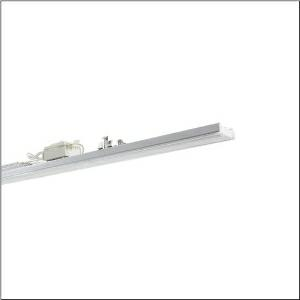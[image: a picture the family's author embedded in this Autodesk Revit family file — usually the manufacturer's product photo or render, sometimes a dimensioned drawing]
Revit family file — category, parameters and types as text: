
# Revit family: licross_r__21_recessed_ho_52te1edn4e5s_6cbf
name_source: partatom
category: Lighting Fixtures
units: mm (PartAtom-declared; Revit-internal decimal feet)

## family parameters
Cut with Voids When Loaded = No
Host = Face
Light Source = No
Part Type = Normal
Room Calculation Point = No
Round Connector Dimension = Use Diameter
Shared = No

## types (1)
- --- (1 x LED, 14620 lm, 84.6 W, 4000K)
    Apparent Load = 85 VA
    CIE Flux Codes = 85 95 99 100 100
    Color Rendering = 80
    Color Temperature = 4000K
    Default Elevation = 1800 mm
    Description = Licross® 21 Recessed HO, luminaire insert, of sheet steel, galvanised, coil coated, white, length: 1.500mm, width: 66mm, height: 67mm, LED rated luminous flux: 14.620lm, light colour: 840, control gear: DALI 2, with plug, 5-pole, with phase selection, mains connection: 220..240V, AC, 50/60Hz, rated input power: 85W, internal wiring halogen-free, primary light control with lens, of plastic, primary optical cover: cover, of PMMA, light emission: direct distribution, primary light characteristic: symmetric, protection rating (complete): IP54, insulation class (complete): insulation class I (protective earthing), certification: CE, ENEC, VDE, UKCA, protection symbol: D if used in an environment with non-conductive dust loads with corresponding accessories, impact resistance: IK06, permissible ambient temperature for indoor applications: -25..+30°C, corresponds to IFS (International Featured Standards) requirements for safety and quality in the food industry, reducing of maximum allowable ambient temperature of 5°C with ceiling mounting, LABS conformity tested according to VDMA 24364:2018-05, packaging unit: 1 piece
    Height = 58 mm
    Lamp = 1 x LED
    Lamp Light Flux = 14620 lm
    Lamp Power = 84.6 W
    Lamp count = 1
    Length = 1500 mm
    Luminous efficacy = 173 lm/W
    Manufacturer = Siteco
    ModVariant = No
    Model = 52TE1EDN4E5S
    Mounting Place = Ceiling
    Mounting Type = Pendant
    Number of Poles = 1
    OnlyDefault = Yes
    Power Factor = 1
    Product Name = Licross® 21 Recessed HO
    Product group = luminaire insert | ceiling pendant
    ProductGroupID = 902
    Protection Class = Protection class I
    Protection Degree = IP 54
    RLX_Detail_Level = 1
    RLX_Emergency_Light_Flux = 0 lm
    RLX_Emergency_Type = 0
    RLX_Emergency_Type_DB = No
    RlxData = <blob elided: 24845 chars, md5=ee6762ab>
    Socket = socket
    Standby Power = 0 W
    System Light Flux = 14620 lm
    System Power = 85 W
    Type Comments = factory setting: luminous flux: 100 % | dim-lin: 254 | 484 mA
    Type Image = l_1296930.jpg
    URL = http://relux.com
    VarID = @adj_146575
    Voltage = 0 V
    Weight = 0.00 kg
    Width = 66 mm

## geometry (parser evidence)
native form markers: Blend x4, Sweep x11
no freeform markers — native parametric forms only
